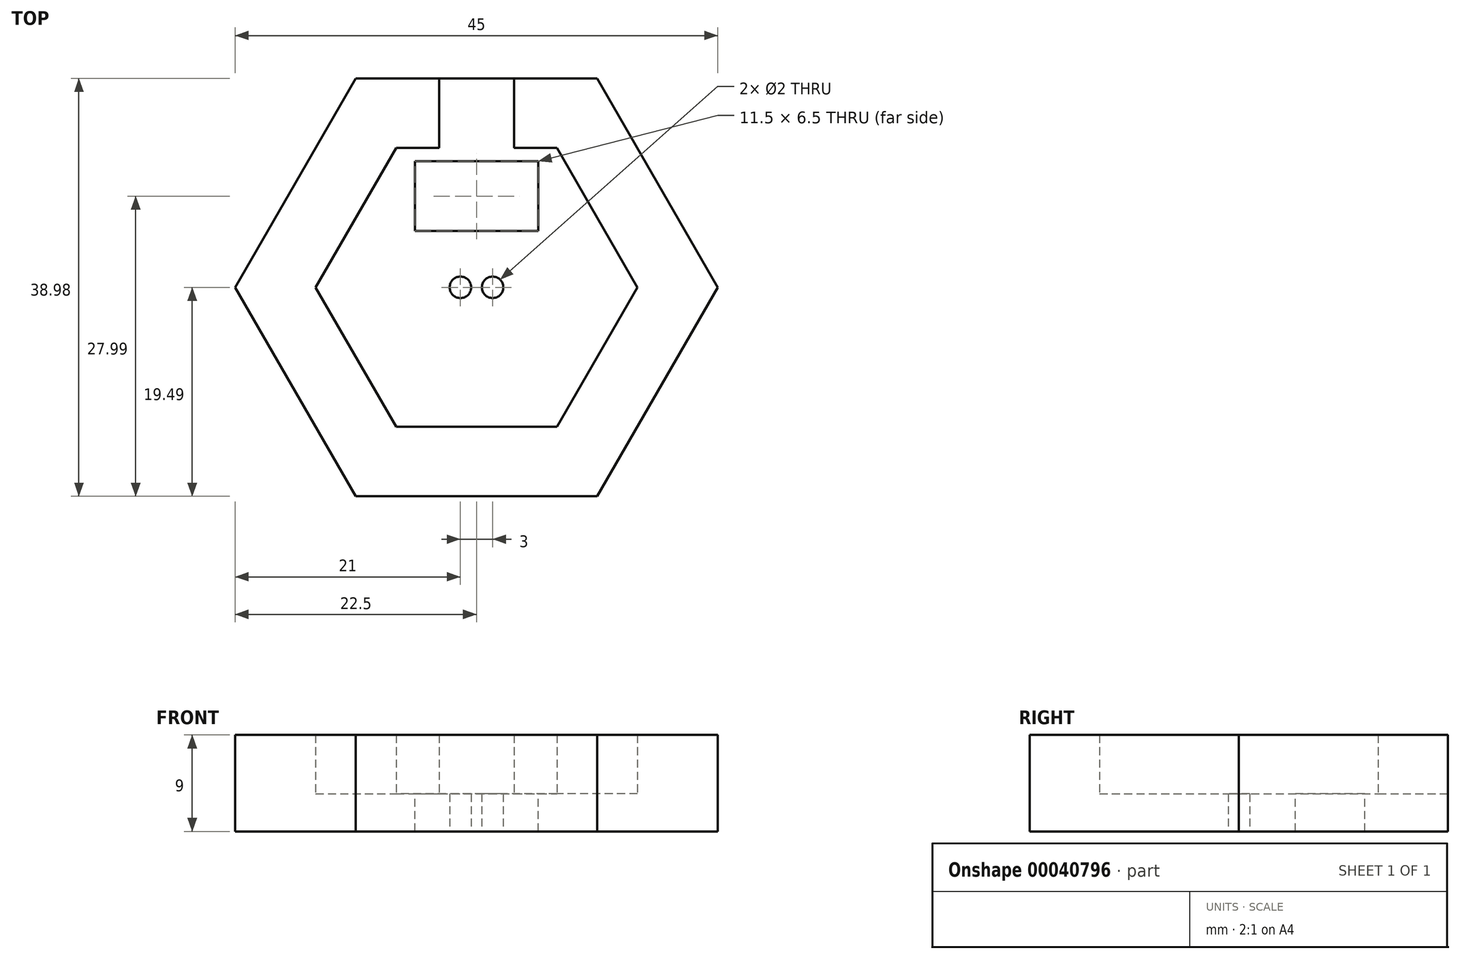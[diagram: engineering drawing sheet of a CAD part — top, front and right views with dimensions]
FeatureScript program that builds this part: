
annotation { "Feature Type Name" : "Feature", "Feature Type Description" : "" }
export const myFeature = defineFeature(function(context is Context, id is Id, definition is map)
    precondition{}
    {
        {
            var Q0;
            Q0=qCreatedBy(makeId("Top.planeOp"),FACE);
            var sketch = newSketch(context, id + "F0", { "sketchPlane" : qUnion([Q0])});
            skCircle(sketch, "E0.cCircle", {"center": v(0, 0) * mm, "radius": 22.5 * mm, "construction": true});
            skLineSegment(sketch, "E0.0", {"start": v(22.5, 0) * mm, "end": v(11.25, -19.49) * mm});
            skLineSegment(sketch, "E0.1", {"start": v(11.25, -19.49) * mm, "end": v(-11.25, -19.49) * mm});
            skLineSegment(sketch, "E0.2", {"start": v(-11.25, -19.49) * mm, "end": v(-22.5, 0) * mm});
            skLineSegment(sketch, "E0.3", {"start": v(-22.5, 0) * mm, "end": v(-11.25, 19.49) * mm});
            skLineSegment(sketch, "E0.4", {"start": v(-11.25, 19.49) * mm, "end": v(11.25, 19.49) * mm});
            skLineSegment(sketch, "E0.5", {"start": v(11.25, 19.49) * mm, "end": v(22.5, 0) * mm});
            skPoint(sketch, "E1", {"position": v(-1.5, 0) * mm});
            skPoint(sketch, "E2", {"position": v(1.5, 0) * mm});
            skCircle(sketch, "E3", {"center": v(-1.5, 0) * mm, "radius": 1 * mm});
            skCircle(sketch, "E4", {"center": v(1.5, 0) * mm, "radius": 1 * mm});
            skSolve(sketch);
        }
        {
            var Q0;
            Q0 = qSketchRegion(id + "F0", true);
            var Q1;
            Q1=makeQuery(id+"F0.imprint","IMPRINT",FACE,{"disambiguationData":[TD([[makeQuery(id+"F0.imprint","IMPRINT",EDGE,{"derivedFrom":sQuery(id+"F0.wireOp",EDGE,"E0.0")}),-1.0]])]});
            extrude(context, id + "F1", {"entities" : qUnion([Q0, Q1]), "depth" : 3.5 * mm});
        }
        {
            var Q0;
            Q0=makeQuery(id+"F1.opExtrude","CAP_FACE",FACE,{"disambiguationData":[OSD([sQuery(id+"F0.wireOp",EDGE,"E0.0"),sQuery(id+"F0.wireOp",EDGE,"E0.1"),sQuery(id+"F0.wireOp",EDGE,"E0.2"),sQuery(id+"F0.wireOp",EDGE,"E0.3"),sQuery(id+"F0.wireOp",EDGE,"E0.4"),sQuery(id+"F0.wireOp",EDGE,"E0.5")])],"isStart":false});
            var sketch = newSketch(context, id + "F2", { "sketchPlane" : qUnion([Q0])});
            skCircle(sketch, "E5.cCircle", {"center": v(0, 0) * mm, "radius": 15 * mm, "construction": true});
            skLineSegment(sketch, "E5.0", {"start": v(15, 0) * mm, "end": v(7.5, -13) * mm});
            skLineSegment(sketch, "E5.1", {"start": v(7.5, -13) * mm, "end": v(-7.5, -13) * mm});
            skLineSegment(sketch, "E5.2", {"start": v(-7.5, -13) * mm, "end": v(-15, 0) * mm});
            skLineSegment(sketch, "E5.3", {"start": v(-15, 0) * mm, "end": v(-7.5, 13) * mm});
            skLineSegment(sketch, "E5.4", {"start": v(-7.5, 13) * mm, "end": v(7.5, 13) * mm});
            skLineSegment(sketch, "E5.5", {"start": v(7.5, 13) * mm, "end": v(15, 0) * mm});
            skLineSegment(sketch, "E6.rect.bottom", {"start": v(3.5, 13) * mm, "end": v(-3.5, 13) * mm});
            skLineSegment(sketch, "E6.rect.top", {"start": v(3.5, 19.49) * mm, "end": v(-3.5, 19.49) * mm});
            skLineSegment(sketch, "E6.rect.left", {"start": v(3.5, 13) * mm, "end": v(3.5, 19.49) * mm});
            skLineSegment(sketch, "E6.rect.right", {"start": v(-3.5, 13) * mm, "end": v(-3.5, 19.49) * mm});
            skPoint(sketch, "E6.rect.middle", {"position": v(0, 16.24) * mm});
            skSolve(sketch);
        }
        {
            var Q0;
            Q0=makeQuery(id+"F2.imprint","IMPRINT",FACE,{"disambiguationData":[TD([[makeQuery(id+"F2.imprint","IMPRINT",EDGE,{"derivedFrom":sQuery(id+"F2.wireOp",EDGE,"E5.0")}),1.0]])]});
            extrude(context, id + "F3", {"entities" : qUnion([Q0]), "operationType" : NewBodyOperationType.ADD, "depth" : 5.5 * mm});
        }
        {
            var Q0;
            Q0=makeQuery(id+"F1.opExtrude","CAP_FACE",FACE,{"disambiguationData":[OSD([sQuery(id+"F0.wireOp",EDGE,"E0.0"),sQuery(id+"F0.wireOp",EDGE,"E0.1"),sQuery(id+"F0.wireOp",EDGE,"E0.2"),sQuery(id+"F0.wireOp",EDGE,"E0.3"),sQuery(id+"F0.wireOp",EDGE,"E0.4"),sQuery(id+"F0.wireOp",EDGE,"E0.5"),sQuery(id+"F0.wireOp",EDGE,"E3"),sQuery(id+"F0.wireOp",EDGE,"E4")])],"isStart":false});
            var sketch = newSketch(context, id + "F4", { "sketchPlane" : qUnion([Q0])});
            skLineSegment(sketch, "E7.rect.bottom", {"start": v(-5.75, 11.75) * mm, "end": v(5.75, 11.75) * mm});
            skLineSegment(sketch, "E7.rect.top", {"start": v(-5.75, 5.25) * mm, "end": v(5.75, 5.25) * mm});
            skLineSegment(sketch, "E7.rect.left", {"start": v(-5.75, 11.75) * mm, "end": v(-5.75, 5.25) * mm});
            skLineSegment(sketch, "E7.rect.right", {"start": v(5.75, 11.75) * mm, "end": v(5.75, 5.25) * mm});
            skPoint(sketch, "E7.rect.middle", {"position": v(0, 8.5) * mm});
            skSolve(sketch);
        }
        {
            var Q0;
            Q0 = qSketchRegion(id + "F4", true);
            extrude(context, id + "F5", {"entities" : qUnion([Q0]), "operationType" : NewBodyOperationType.REMOVE, "endBound" : BoundingType.UP_TO_NEXT, "oppositeDirection" : true, "depth" : 5 * mm});
        }
    });
